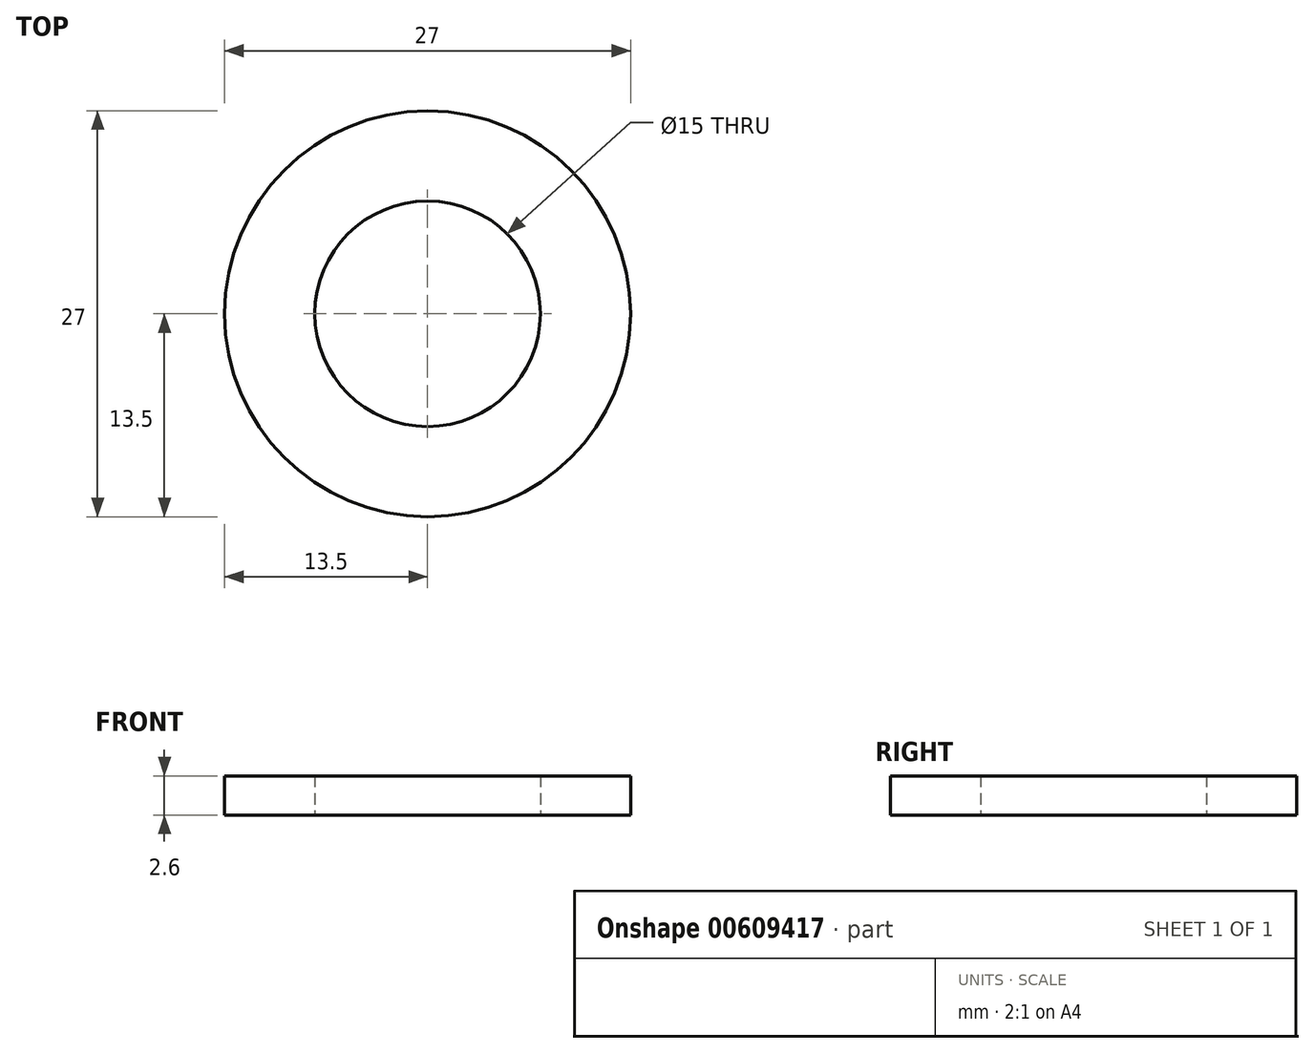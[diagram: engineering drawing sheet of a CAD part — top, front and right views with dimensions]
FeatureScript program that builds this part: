
annotation { "Feature Type Name" : "Feature", "Feature Type Description" : "" }
export const myFeature = defineFeature(function(context is Context, id is Id, definition is map)
    precondition{}
    {
        {
            var Q0;
            Q0=qCreatedBy(makeId("Top.planeOp"),FACE);
            var sketch = newSketch(context, id + "F0", { "sketchPlane" : qUnion([Q0])});
            skCircle(sketch, "E0", {"center": v(0, 0) * mm, "radius": 7.5 * mm});
            skCircle(sketch, "E1", {"center": v(0, 0) * mm, "radius": 13.5 * mm});
            skSolve(sketch);
        }
        {
            var Q0;
            Q0 = qSketchRegion(id + "F0", true);
            extrude(context, id + "F1", {"entities" : qUnion([Q0]), "depth" : 2.6 * mm, "offsetDistance" : 25 * mm});
        }
    });
